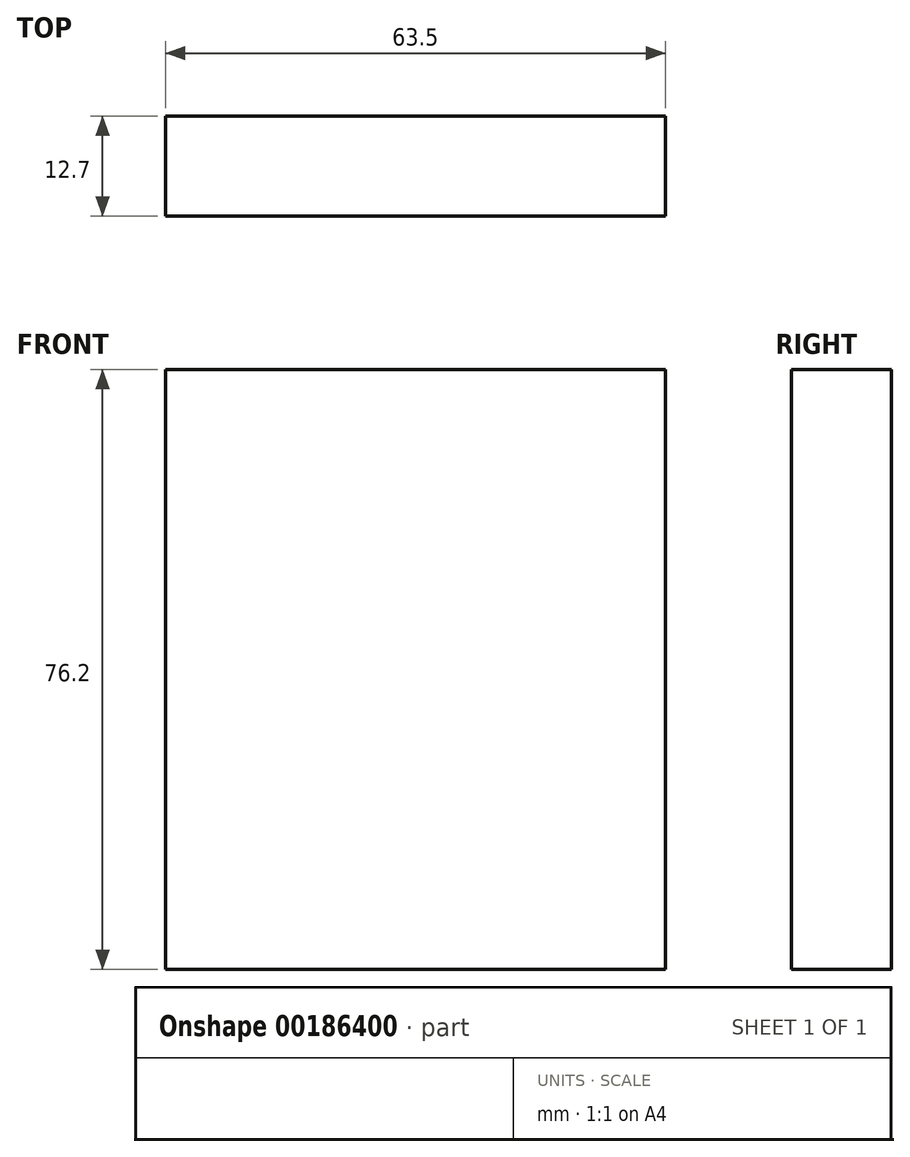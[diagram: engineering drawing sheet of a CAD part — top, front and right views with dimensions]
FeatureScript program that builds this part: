
annotation { "Feature Type Name" : "Feature", "Feature Type Description" : "" }
export const myFeature = defineFeature(function(context is Context, id is Id, definition is map)
    precondition{}
    {
        {
            var Q0;
            Q0=qCreatedBy(makeId("Right.planeOp"),FACE);
            var sketch = newSketch(context, id + "F0", { "sketchPlane" : qUnion([Q0])});
            skLineSegment(sketch, "E0.bottom", {"start": v(-188.87, 90.8) * mm, "end": v(-176.17, 90.8) * mm});
            skLineSegment(sketch, "E0.top", {"start": v(-188.87, 14.6) * mm, "end": v(-176.17, 14.6) * mm});
            skLineSegment(sketch, "E0.left", {"start": v(-188.87, 90.8) * mm, "end": v(-188.87, 14.6) * mm});
            skLineSegment(sketch, "E0.right", {"start": v(-176.17, 90.8) * mm, "end": v(-176.17, 14.6) * mm});
            skSolve(sketch);
        }
        {
            var Q0;
            Q0=makeQuery(id+"F0.imprint","IMPRINT",FACE,{"disambiguationData":[TD([[makeQuery(id+"F0.imprint","IMPRINT",EDGE,{"derivedFrom":sQuery(id+"F0.wireOp",EDGE,"E0.bottom")}),-1.0]])]});
            extrude(context, id + "F1", {"entities" : qUnion([Q0]), "depth" : 63.5 * mm});
        }
    });
